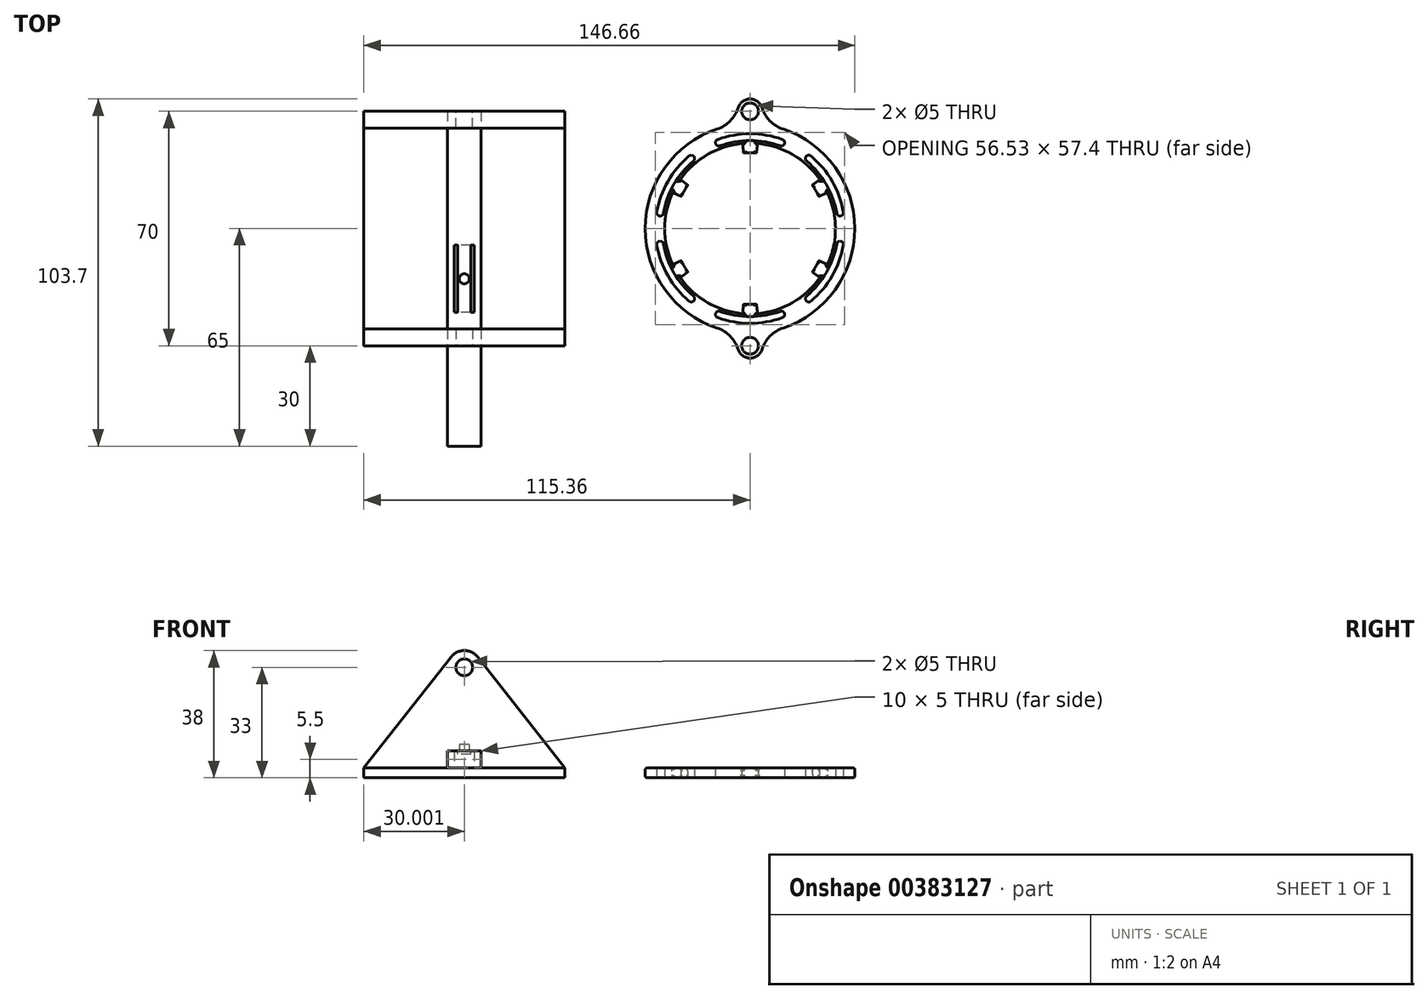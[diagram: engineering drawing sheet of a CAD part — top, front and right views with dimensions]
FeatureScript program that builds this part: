
annotation { "Feature Type Name" : "Feature", "Feature Type Description" : "" }
export const myFeature = defineFeature(function(context is Context, id is Id, definition is map)
    precondition{}
    {
        {
            var Q0;
            Q0=qCreatedBy(makeId("Top.planeOp"),FACE);
            var sketch = newSketch(context, id + "F0", { "sketchPlane" : qUnion([Q0])});
            skArc(sketch, "E0", {"start": v(-2.22, 25.4) * mm, "mid": v(-12.75, 22.08) * mm, "end": v(-20.89, 14.63) * mm});
            skArc(sketch, "E1", {"start": v(-9.89, 29.7) * mm, "mid": v(-31.3, 0) * mm, "end": v(-9.89, -29.7) * mm});
            skArc(sketch, "E2", {"start": v(1.97, 22.56) * mm, "mid": v(0, 22.65) * mm, "end": v(-1.97, 22.56) * mm});
            skArc(sketch, "E3", {"start": v(9, 24.71) * mm, "mid": v(0, 26.3) * mm, "end": v(-9, 24.71) * mm});
            skArc(sketch, "E4", {"start": v(9.68, 26.6) * mm, "mid": v(0, 28.3) * mm, "end": v(-9.68, 26.6) * mm});
            skLineSegment(sketch, "E5", {"start": v(0, 0) * mm, "end": v(-1.97, 22.56) * mm, "construction": true});
            skLineSegment(sketch, "E6", {"start": v(-1.97, 22.56) * mm, "end": v(-2.22, 25.4) * mm});
            skArc(sketch, "E7", {"start": v(-9.68, 26.6) * mm, "mid": v(-10.28, 25.31) * mm, "end": v(-9, 24.71) * mm});
            skLineSegment(sketch, "E8.MirrorCS", {"start": v(1.97, 22.56) * mm, "end": v(2.22, 25.4) * mm});
            skArc(sketch, "E9.MirrorCS", {"start": v(9.68, 26.6) * mm, "mid": v(10.28, 25.31) * mm, "end": v(9, 24.71) * mm});
            skLineSegment(sketch, "E10", {"start": v(-9.34, 25.65) * mm, "end": v(0, 0) * mm, "construction": true});
            skLineSegment(sketch, "E11", {"start": v(0, 0) * mm, "end": v(9.34, 25.65) * mm, "construction": true});
            skLineSegment(sketch, "E12", {"start": v(1.97, 22.56) * mm, "end": v(0, 0) * mm, "construction": true});
            skLineSegment(sketch, "E13.1.0", {"start": v(-20.53, 9.57) * mm, "end": v(-23.11, 10.78) * mm});
            skArc(sketch, "E13.1.1", {"start": v(-18.55, 13) * mm, "mid": v(-19.62, 11.33) * mm, "end": v(-20.53, 9.57) * mm});
            skLineSegment(sketch, "E13.1.2", {"start": v(-18.55, 13) * mm, "end": v(-20.89, 14.63) * mm});
            skArc(sketch, "E13.1.3", {"start": v(-16.9, 20.15) * mm, "mid": v(-22.78, 13.15) * mm, "end": v(-25.9, 4.57) * mm});
            skArc(sketch, "E13.1.4", {"start": v(-27.87, 4.91) * mm, "mid": v(-27.06, 3.76) * mm, "end": v(-25.9, 4.57) * mm});
            skArc(sketch, "E13.1.5", {"start": v(-18.2, 21.68) * mm, "mid": v(-24.5, 14.15) * mm, "end": v(-27.87, 4.91) * mm});
            skArc(sketch, "E13.1.6", {"start": v(-18.2, 21.68) * mm, "mid": v(-16.78, 21.56) * mm, "end": v(-16.9, 20.15) * mm});
            skLineSegment(sketch, "E13.2.0", {"start": v(-18.55, -13) * mm, "end": v(-20.89, -14.63) * mm});
            skArc(sketch, "E13.2.1", {"start": v(-20.53, -9.57) * mm, "mid": v(-19.62, -11.32) * mm, "end": v(-18.55, -13) * mm});
            skLineSegment(sketch, "E13.2.2", {"start": v(-20.53, -9.57) * mm, "end": v(-23.11, -10.78) * mm});
            skArc(sketch, "E13.2.3", {"start": v(-25.9, -4.57) * mm, "mid": v(-22.78, -13.15) * mm, "end": v(-16.9, -20.15) * mm});
            skArc(sketch, "E13.2.4", {"start": v(-18.2, -21.68) * mm, "mid": v(-16.78, -21.56) * mm, "end": v(-16.9, -20.15) * mm});
            skArc(sketch, "E13.2.5", {"start": v(-27.87, -4.91) * mm, "mid": v(-24.5, -14.15) * mm, "end": v(-18.2, -21.68) * mm});
            skArc(sketch, "E13.2.6", {"start": v(-27.87, -4.91) * mm, "mid": v(-27.06, -3.76) * mm, "end": v(-25.9, -4.57) * mm});
            skLineSegment(sketch, "E13.3.0", {"start": v(1.97, -22.56) * mm, "end": v(2.22, -25.4) * mm});
            skArc(sketch, "E13.3.1", {"start": v(-1.97, -22.56) * mm, "mid": v(0, -22.65) * mm, "end": v(1.97, -22.56) * mm});
            skLineSegment(sketch, "E13.3.2", {"start": v(-1.97, -22.56) * mm, "end": v(-2.22, -25.4) * mm});
            skArc(sketch, "E13.3.3", {"start": v(-9, -24.71) * mm, "mid": v(0, -26.3) * mm, "end": v(9, -24.71) * mm});
            skArc(sketch, "E13.3.4", {"start": v(9.68, -26.6) * mm, "mid": v(10.28, -25.31) * mm, "end": v(9, -24.71) * mm});
            skArc(sketch, "E13.3.5", {"start": v(-9.68, -26.6) * mm, "mid": v(0, -28.3) * mm, "end": v(9.68, -26.6) * mm});
            skArc(sketch, "E13.3.6", {"start": v(-9.68, -26.6) * mm, "mid": v(-10.28, -25.31) * mm, "end": v(-9, -24.71) * mm});
            skLineSegment(sketch, "E13.4.0", {"start": v(20.53, -9.57) * mm, "end": v(23.11, -10.78) * mm});
            skArc(sketch, "E13.4.1", {"start": v(18.55, -13) * mm, "mid": v(19.62, -11.33) * mm, "end": v(20.53, -9.57) * mm});
            skLineSegment(sketch, "E13.4.2", {"start": v(18.55, -13) * mm, "end": v(20.89, -14.63) * mm});
            skArc(sketch, "E13.4.3", {"start": v(16.9, -20.15) * mm, "mid": v(22.78, -13.15) * mm, "end": v(25.9, -4.57) * mm});
            skArc(sketch, "E13.4.4", {"start": v(27.87, -4.91) * mm, "mid": v(27.06, -3.76) * mm, "end": v(25.9, -4.57) * mm});
            skArc(sketch, "E13.4.5", {"start": v(18.2, -21.68) * mm, "mid": v(24.5, -14.15) * mm, "end": v(27.87, -4.91) * mm});
            skArc(sketch, "E13.4.6", {"start": v(18.2, -21.68) * mm, "mid": v(16.78, -21.56) * mm, "end": v(16.9, -20.15) * mm});
            skLineSegment(sketch, "E13.5.0", {"start": v(18.55, 13) * mm, "end": v(20.89, 14.63) * mm});
            skArc(sketch, "E13.5.1", {"start": v(20.53, 9.57) * mm, "mid": v(19.62, 11.33) * mm, "end": v(18.55, 13) * mm});
            skLineSegment(sketch, "E13.5.2", {"start": v(20.53, 9.57) * mm, "end": v(23.11, 10.78) * mm});
            skArc(sketch, "E13.5.3", {"start": v(25.9, 4.57) * mm, "mid": v(22.78, 13.15) * mm, "end": v(16.9, 20.15) * mm});
            skArc(sketch, "E13.5.4", {"start": v(18.2, 21.68) * mm, "mid": v(16.78, 21.56) * mm, "end": v(16.9, 20.15) * mm});
            skArc(sketch, "E13.5.5", {"start": v(27.87, 4.91) * mm, "mid": v(24.5, 14.15) * mm, "end": v(18.2, 21.68) * mm});
            skArc(sketch, "E13.5.6", {"start": v(27.87, 4.91) * mm, "mid": v(27.06, 3.76) * mm, "end": v(25.9, 4.57) * mm});
            skArc(sketch, "E14.trimOffspring", {"start": v(20.89, 14.63) * mm, "mid": v(12.75, 22.08) * mm, "end": v(2.22, 25.4) * mm});
            skArc(sketch, "E15.trimOffspring", {"start": v(-23.11, 10.78) * mm, "mid": v(-25.5, 0) * mm, "end": v(-23.11, -10.78) * mm});
            skArc(sketch, "E16.trimOffspring", {"start": v(-20.89, -14.63) * mm, "mid": v(-12.75, -22.08) * mm, "end": v(-2.22, -25.4) * mm});
            skArc(sketch, "E17.trimOffspring", {"start": v(23.11, -10.78) * mm, "mid": v(25.5, 0) * mm, "end": v(23.11, 10.78) * mm});
            skArc(sketch, "E18.trimOffspring", {"start": v(2.22, -25.4) * mm, "mid": v(12.75, -22.08) * mm, "end": v(20.89, -14.63) * mm});
            skArc(sketch, "E19", {"start": v(3.52, 36.13) * mm, "mid": v(0, 38.7) * mm, "end": v(-3.52, 36.13) * mm});
            skCircle(sketch, "E20", {"center": v(0, 35) * mm, "radius": 2.5 * mm});
            skArc(sketch, "E21", {"start": v(-9.89, 29.7) * mm, "mid": v(-5.94, 32.15) * mm, "end": v(-3.52, 36.13) * mm});
            skArc(sketch, "E22.MirrorCS", {"start": v(9.89, 29.7) * mm, "mid": v(5.94, 32.15) * mm, "end": v(3.52, 36.13) * mm});
            skArc(sketch, "E23.MirrorCS", {"start": v(-9.89, -29.7) * mm, "mid": v(-5.94, -32.15) * mm, "end": v(-3.52, -36.13) * mm});
            skArc(sketch, "E24.MirrorCS", {"start": v(3.52, -36.13) * mm, "mid": v(0, -38.7) * mm, "end": v(-3.52, -36.13) * mm});
            skArc(sketch, "E25.MirrorCS", {"start": v(9.89, -29.7) * mm, "mid": v(5.94, -32.15) * mm, "end": v(3.52, -36.13) * mm});
            skCircle(sketch, "E26.MirrorC", {"center": v(0, -35) * mm, "radius": 2.5 * mm});
            skArc(sketch, "E27.trimOffspring", {"start": v(9.89, -29.7) * mm, "mid": v(31.3, 0) * mm, "end": v(9.89, 29.7) * mm});
            skSolve(sketch);
        }
        {
            var Q0;
            Q0=makeQuery(id+"F0.imprint","IMPRINT",FACE,{"disambiguationData":[TD([[makeQuery(id+"F0.imprint","IMPRINT",EDGE,{"derivedFrom":sQuery(id+"F0.wireOp",EDGE,"E0")}),-1.0]])]});
            extrude(context, id + "F1", {"entities" : qUnion([Q0]), "depth" : 1.5 * mm});
        }
        {
            var Q0;
            Q0=makeQuery(id+"F1.opExtrude","CAP_EDGE",EDGE,{"disambiguationData":[OSD([sQuery(id+"F0.wireOp",EDGE,"E6")])],"isStart":true});
            var Q1;
            Q1=makeQuery(id+"F1.opExtrude","CAP_EDGE",EDGE,{"disambiguationData":[OSD([sQuery(id+"F0.wireOp",EDGE,"E8.MirrorCS")])],"isStart":true});
            var Q2;
            Q2=makeQuery(id+"F1.opExtrude","CAP_EDGE",EDGE,{"disambiguationData":[OSD([sQuery(id+"F0.wireOp",EDGE,"E13.5.0")])],"isStart":true});
            var Q3;
            Q3=makeQuery(id+"F1.opExtrude","CAP_EDGE",EDGE,{"disambiguationData":[OSD([sQuery(id+"F0.wireOp",EDGE,"E13.5.2")])],"isStart":true});
            var Q4;
            Q4=makeQuery(id+"F1.opExtrude","CAP_EDGE",EDGE,{"disambiguationData":[OSD([sQuery(id+"F0.wireOp",EDGE,"E13.4.2")])],"isStart":true});
            var Q5;
            Q5=makeQuery(id+"F1.opExtrude","CAP_EDGE",EDGE,{"disambiguationData":[OSD([sQuery(id+"F0.wireOp",EDGE,"E13.3.2")])],"isStart":true});
            var Q6;
            Q6=makeQuery(id+"F1.opExtrude","CAP_EDGE",EDGE,{"disambiguationData":[OSD([sQuery(id+"F0.wireOp",EDGE,"E13.4.0")])],"isStart":true});
            var Q7;
            Q7=makeQuery(id+"F1.opExtrude","CAP_EDGE",EDGE,{"disambiguationData":[OSD([sQuery(id+"F0.wireOp",EDGE,"E13.1.2")])],"isStart":true});
            var Q8;
            Q8=makeQuery(id+"F1.opExtrude","CAP_EDGE",EDGE,{"disambiguationData":[OSD([sQuery(id+"F0.wireOp",EDGE,"E13.2.2")])],"isStart":true});
            var Q9;
            Q9=makeQuery(id+"F1.opExtrude","CAP_EDGE",EDGE,{"disambiguationData":[OSD([sQuery(id+"F0.wireOp",EDGE,"E13.3.0")])],"isStart":true});
            var Q10;
            Q10=makeQuery(id+"F1.opExtrude","CAP_EDGE",EDGE,{"disambiguationData":[OSD([sQuery(id+"F0.wireOp",EDGE,"E13.2.0")])],"isStart":true});
            var Q11;
            Q11=makeQuery(id+"F1.opExtrude","CAP_EDGE",EDGE,{"disambiguationData":[OSD([sQuery(id+"F0.wireOp",EDGE,"E13.1.0")])],"isStart":true});
            fillet(context, id + "F2", {"entities" : qUnion([Q0, Q1, Q2, Q3, Q4, Q5, Q6, Q7, Q8, Q9, Q10, Q11]), "radius" : 1 * mm, "tangentPropagation" : true, "allowEdgeOverflow" : false});
        }
        {
            var Q0;
            Q0=makeQuery(id+"F1.opExtrude","CAP_EDGE",EDGE,{"disambiguationData":[OSD([sQuery(id+"F0.wireOp",EDGE,"E13.3.1")])],"isStart":true});
            var Q1;
            Q1=makeQuery(id+"F1.opExtrude","CAP_EDGE",EDGE,{"disambiguationData":[OSD([sQuery(id+"F0.wireOp",EDGE,"E13.4.1")])],"isStart":true});
            var Q2;
            Q2=makeQuery(id+"F1.opExtrude","CAP_EDGE",EDGE,{"disambiguationData":[OSD([sQuery(id+"F0.wireOp",EDGE,"E13.5.1")])],"isStart":true});
            var Q3;
            Q3=makeQuery(id+"F1.opExtrude","CAP_EDGE",EDGE,{"disambiguationData":[OSD([sQuery(id+"F0.wireOp",EDGE,"E2")])],"isStart":true});
            var Q4;
            Q4=makeQuery(id+"F1.opExtrude","CAP_EDGE",EDGE,{"disambiguationData":[OSD([sQuery(id+"F0.wireOp",EDGE,"E13.1.1")])],"isStart":true});
            var Q5;
            Q5=makeQuery(id+"F1.opExtrude","CAP_EDGE",EDGE,{"disambiguationData":[OSD([sQuery(id+"F0.wireOp",EDGE,"E13.2.1")])],"isStart":true});
            fillet(context, id + "F3", {"entities" : qUnion([Q0, Q1, Q2, Q3, Q4, Q5]), "radius" : 0.2 * mm, "tangentPropagation" : true, "allowEdgeOverflow" : false});
        }
        {
            var Q0;
            Q0=makeQuery(id+"F1.opExtrude","CAP_EDGE",EDGE,{"disambiguationData":[OSD([sQuery(id+"F0.wireOp",EDGE,"E14.trimOffspring")])],"isStart":true});
            var Q1;
            Q1=makeQuery(id+"F1.opExtrude","CAP_EDGE",EDGE,{"disambiguationData":[OSD([sQuery(id+"F0.wireOp",EDGE,"E0")])],"isStart":true});
            var Q2;
            Q2=makeQuery(id+"F1.opExtrude","CAP_EDGE",EDGE,{"disambiguationData":[OSD([sQuery(id+"F0.wireOp",EDGE,"E15.trimOffspring")])],"isStart":true});
            var Q3;
            Q3=makeQuery(id+"F1.opExtrude","CAP_EDGE",EDGE,{"disambiguationData":[OSD([sQuery(id+"F0.wireOp",EDGE,"E16.trimOffspring")])],"isStart":true});
            var Q4;
            Q4=makeQuery(id+"F1.opExtrude","CAP_EDGE",EDGE,{"disambiguationData":[OSD([sQuery(id+"F0.wireOp",EDGE,"E18.trimOffspring")])],"isStart":true});
            var Q5;
            Q5=makeQuery(id+"F1.opExtrude","CAP_EDGE",EDGE,{"disambiguationData":[OSD([sQuery(id+"F0.wireOp",EDGE,"E17.trimOffspring")])],"isStart":true});
            var Q6;
            Q6=makeQuery(id+"F1.opExtrude","CAP_EDGE",EDGE,{"disambiguationData":[OSD([sQuery(id+"F0.wireOp",EDGE,"E13.4.5")])],"isStart":true});
            var Q7;
            Q7=makeQuery(id+"F1.opExtrude","CAP_EDGE",EDGE,{"disambiguationData":[OSD([sQuery(id+"F0.wireOp",EDGE,"E13.3.3")])],"isStart":true});
            var Q8;
            Q8=makeQuery(id+"F1.opExtrude","CAP_EDGE",EDGE,{"disambiguationData":[OSD([sQuery(id+"F0.wireOp",EDGE,"E13.2.5")])],"isStart":true});
            var Q9;
            Q9=makeQuery(id+"F1.opExtrude","CAP_EDGE",EDGE,{"disambiguationData":[OSD([sQuery(id+"F0.wireOp",EDGE,"E13.1.5")])],"isStart":true});
            var Q10;
            Q10=makeQuery(id+"F1.opExtrude","CAP_EDGE",EDGE,{"disambiguationData":[OSD([sQuery(id+"F0.wireOp",EDGE,"E3")])],"isStart":true});
            var Q11;
            Q11=makeQuery(id+"F1.opExtrude","CAP_EDGE",EDGE,{"disambiguationData":[OSD([sQuery(id+"F0.wireOp",EDGE,"E13.5.3")])],"isStart":true});
            fillet(context, id + "F4", {"entities" : qUnion([Q0, Q1, Q2, Q3, Q4, Q5, Q6, Q7, Q8, Q9, Q10, Q11]), "radius" : 0.4 * mm, "tangentPropagation" : true, "allowEdgeOverflow" : false});
        }
        {
            var Q0;
            Q0=makeQuery(id+"F1.opExtrude","SWEPT_EDGE",EDGE,{"disambiguationData":[OSD([sQuery(id+"F0.wireOp",EDGE,"E13.5.0"),sQuery(id+"F0.wireOp",EDGE,"E14.trimOffspring")])]});
            var Q1;
            Q1=makeQuery(id+"F1.opExtrude","SWEPT_EDGE",EDGE,{"disambiguationData":[OSD([sQuery(id+"F0.wireOp",EDGE,"E13.4.0"),sQuery(id+"F0.wireOp",EDGE,"E17.trimOffspring")])]});
            var Q2;
            Q2=makeQuery(id+"F1.opExtrude","SWEPT_EDGE",EDGE,{"disambiguationData":[OSD([sQuery(id+"F0.wireOp",EDGE,"E13.4.2"),sQuery(id+"F0.wireOp",EDGE,"E18.trimOffspring")])]});
            var Q3;
            Q3=makeQuery(id+"F1.opExtrude","SWEPT_EDGE",EDGE,{"disambiguationData":[OSD([sQuery(id+"F0.wireOp",EDGE,"E13.3.2"),sQuery(id+"F0.wireOp",EDGE,"E16.trimOffspring")])]});
            var Q4;
            Q4=makeQuery(id+"F1.opExtrude","SWEPT_EDGE",EDGE,{"disambiguationData":[OSD([sQuery(id+"F0.wireOp",EDGE,"E13.2.2"),sQuery(id+"F0.wireOp",EDGE,"E15.trimOffspring")])]});
            var Q5;
            Q5=makeQuery(id+"F1.opExtrude","SWEPT_EDGE",EDGE,{"disambiguationData":[OSD([sQuery(id+"F0.wireOp",EDGE,"E13.3.0"),sQuery(id+"F0.wireOp",EDGE,"E18.trimOffspring")])]});
            var Q6;
            Q6=makeQuery(id+"F1.opExtrude","SWEPT_EDGE",EDGE,{"disambiguationData":[OSD([sQuery(id+"F0.wireOp",EDGE,"E13.2.0"),sQuery(id+"F0.wireOp",EDGE,"E16.trimOffspring")])]});
            var Q7;
            Q7=makeQuery(id+"F1.opExtrude","SWEPT_EDGE",EDGE,{"disambiguationData":[OSD([sQuery(id+"F0.wireOp",EDGE,"E0"),sQuery(id+"F0.wireOp",EDGE,"E13.1.2")])]});
            var Q8;
            Q8=makeQuery(id+"F1.opExtrude","SWEPT_EDGE",EDGE,{"disambiguationData":[OSD([sQuery(id+"F0.wireOp",EDGE,"E8.MirrorCS"),sQuery(id+"F0.wireOp",EDGE,"E14.trimOffspring")])]});
            var Q9;
            Q9=makeQuery(id+"F1.opExtrude","SWEPT_EDGE",EDGE,{"disambiguationData":[OSD([sQuery(id+"F0.wireOp",EDGE,"E13.1.0"),sQuery(id+"F0.wireOp",EDGE,"E15.trimOffspring")])]});
            var Q10;
            Q10=makeQuery(id+"F1.opExtrude","SWEPT_EDGE",EDGE,{"disambiguationData":[OSD([sQuery(id+"F0.wireOp",EDGE,"E0"),sQuery(id+"F0.wireOp",EDGE,"E6")])]});
            var Q11;
            Q11=makeQuery(id+"F1.opExtrude","SWEPT_EDGE",EDGE,{"disambiguationData":[OSD([sQuery(id+"F0.wireOp",EDGE,"E13.5.2"),sQuery(id+"F0.wireOp",EDGE,"E17.trimOffspring")])]});
            fillet(context, id + "F5", {"entities" : qUnion([Q0, Q1, Q2, Q3, Q4, Q5, Q6, Q7, Q8, Q9, Q10, Q11]), "radius" : 0.5 * mm, "tangentPropagation" : true, "allowEdgeOverflow" : false});
        }
        {
            var Q0;
            Q0=makeQuery(id+"F1.opExtrude","CAP_EDGE",EDGE,{"disambiguationData":[OSD([sQuery(id+"F0.wireOp",EDGE,"E27.trimOffspring")])],"isStart":true});
            var Q1;
            Q1=makeQuery(id+"F1.opExtrude","CAP_EDGE",EDGE,{"disambiguationData":[OSD([sQuery(id+"F0.wireOp",EDGE,"E26.MirrorC")])],"isStart":true});
            var Q2;
            Q2=makeQuery(id+"F1.opExtrude","CAP_EDGE",EDGE,{"disambiguationData":[OSD([sQuery(id+"F0.wireOp",EDGE,"E20")])],"isStart":true});
            fillet(context, id + "F6", {"entities" : qUnion([Q0, Q1, Q2]), "radius" : 0.6 * mm, "tangentPropagation" : true, "allowEdgeOverflow" : false});
        }
        {
            var Q0;
            Q0=makeQuery(id+"F1.opExtrude","SWEPT_BODY",BODY,{"disambiguationData":[OSD([sQuery(id+"F0.wireOp",EDGE,"E0"),sQuery(id+"F0.wireOp",EDGE,"E1"),sQuery(id+"F0.wireOp",EDGE,"E2"),sQuery(id+"F0.wireOp",EDGE,"E3"),sQuery(id+"F0.wireOp",EDGE,"E4"),sQuery(id+"F0.wireOp",EDGE,"E6"),sQuery(id+"F0.wireOp",EDGE,"E7"),sQuery(id+"F0.wireOp",EDGE,"E8.MirrorCS"),sQuery(id+"F0.wireOp",EDGE,"E9.MirrorCS"),sQuery(id+"F0.wireOp",EDGE,"E13.1.0"),sQuery(id+"F0.wireOp",EDGE,"E13.1.1"),sQuery(id+"F0.wireOp",EDGE,"E13.1.2"),sQuery(id+"F0.wireOp",EDGE,"E13.1.3"),sQuery(id+"F0.wireOp",EDGE,"E13.1.4"),sQuery(id+"F0.wireOp",EDGE,"E13.1.5"),sQuery(id+"F0.wireOp",EDGE,"E13.1.6"),sQuery(id+"F0.wireOp",EDGE,"E13.2.0"),sQuery(id+"F0.wireOp",EDGE,"E13.2.1"),sQuery(id+"F0.wireOp",EDGE,"E13.2.2"),sQuery(id+"F0.wireOp",EDGE,"E13.2.3"),sQuery(id+"F0.wireOp",EDGE,"E13.2.4"),sQuery(id+"F0.wireOp",EDGE,"E13.2.5"),sQuery(id+"F0.wireOp",EDGE,"E13.2.6"),sQuery(id+"F0.wireOp",EDGE,"E13.3.0"),sQuery(id+"F0.wireOp",EDGE,"E13.3.1"),sQuery(id+"F0.wireOp",EDGE,"E13.3.2"),sQuery(id+"F0.wireOp",EDGE,"E13.3.3"),sQuery(id+"F0.wireOp",EDGE,"E13.3.4"),sQuery(id+"F0.wireOp",EDGE,"E13.3.5"),sQuery(id+"F0.wireOp",EDGE,"E13.3.6"),sQuery(id+"F0.wireOp",EDGE,"E13.4.0"),sQuery(id+"F0.wireOp",EDGE,"E13.4.1"),sQuery(id+"F0.wireOp",EDGE,"E13.4.2"),sQuery(id+"F0.wireOp",EDGE,"E13.4.3"),sQuery(id+"F0.wireOp",EDGE,"E13.4.4"),sQuery(id+"F0.wireOp",EDGE,"E13.4.5"),sQuery(id+"F0.wireOp",EDGE,"E13.4.6"),sQuery(id+"F0.wireOp",EDGE,"E13.5.0"),sQuery(id+"F0.wireOp",EDGE,"E13.5.1"),sQuery(id+"F0.wireOp",EDGE,"E13.5.2"),sQuery(id+"F0.wireOp",EDGE,"E13.5.3"),sQuery(id+"F0.wireOp",EDGE,"E13.5.4"),sQuery(id+"F0.wireOp",EDGE,"E13.5.5"),sQuery(id+"F0.wireOp",EDGE,"E13.5.6"),sQuery(id+"F0.wireOp",EDGE,"E14.trimOffspring"),sQuery(id+"F0.wireOp",EDGE,"E15.trimOffspring"),sQuery(id+"F0.wireOp",EDGE,"E16.trimOffspring"),sQuery(id+"F0.wireOp",EDGE,"E17.trimOffspring"),sQuery(id+"F0.wireOp",EDGE,"E18.trimOffspring"),sQuery(id+"F0.wireOp",EDGE,"E19"),sQuery(id+"F0.wireOp",EDGE,"E20"),sQuery(id+"F0.wireOp",EDGE,"E21"),sQuery(id+"F0.wireOp",EDGE,"E22.MirrorCS"),sQuery(id+"F0.wireOp",EDGE,"E23.MirrorCS"),sQuery(id+"F0.wireOp",EDGE,"E24.MirrorCS"),sQuery(id+"F0.wireOp",EDGE,"E25.MirrorCS"),sQuery(id+"F0.wireOp",EDGE,"E26.MirrorC"),sQuery(id+"F0.wireOp",EDGE,"E27.trimOffspring")])]});
            var Q1;
            Q1=makeQuery(id+"F1.opExtrude","CAP_FACE",FACE,{"disambiguationData":[OSD([sQuery(id+"F0.wireOp",EDGE,"E0"),sQuery(id+"F0.wireOp",EDGE,"E1"),sQuery(id+"F0.wireOp",EDGE,"E2"),sQuery(id+"F0.wireOp",EDGE,"E3"),sQuery(id+"F0.wireOp",EDGE,"E4"),sQuery(id+"F0.wireOp",EDGE,"E6"),sQuery(id+"F0.wireOp",EDGE,"E7"),sQuery(id+"F0.wireOp",EDGE,"E8.MirrorCS"),sQuery(id+"F0.wireOp",EDGE,"E9.MirrorCS"),sQuery(id+"F0.wireOp",EDGE,"E13.1.0"),sQuery(id+"F0.wireOp",EDGE,"E13.1.1"),sQuery(id+"F0.wireOp",EDGE,"E13.1.2"),sQuery(id+"F0.wireOp",EDGE,"E13.1.3"),sQuery(id+"F0.wireOp",EDGE,"E13.1.4"),sQuery(id+"F0.wireOp",EDGE,"E13.1.5"),sQuery(id+"F0.wireOp",EDGE,"E13.1.6"),sQuery(id+"F0.wireOp",EDGE,"E13.2.0"),sQuery(id+"F0.wireOp",EDGE,"E13.2.1"),sQuery(id+"F0.wireOp",EDGE,"E13.2.2"),sQuery(id+"F0.wireOp",EDGE,"E13.2.3"),sQuery(id+"F0.wireOp",EDGE,"E13.2.4"),sQuery(id+"F0.wireOp",EDGE,"E13.2.5"),sQuery(id+"F0.wireOp",EDGE,"E13.2.6"),sQuery(id+"F0.wireOp",EDGE,"E13.3.0"),sQuery(id+"F0.wireOp",EDGE,"E13.3.1"),sQuery(id+"F0.wireOp",EDGE,"E13.3.2"),sQuery(id+"F0.wireOp",EDGE,"E13.3.3"),sQuery(id+"F0.wireOp",EDGE,"E13.3.4"),sQuery(id+"F0.wireOp",EDGE,"E13.3.5"),sQuery(id+"F0.wireOp",EDGE,"E13.3.6"),sQuery(id+"F0.wireOp",EDGE,"E13.4.0"),sQuery(id+"F0.wireOp",EDGE,"E13.4.1"),sQuery(id+"F0.wireOp",EDGE,"E13.4.2"),sQuery(id+"F0.wireOp",EDGE,"E13.4.3"),sQuery(id+"F0.wireOp",EDGE,"E13.4.4"),sQuery(id+"F0.wireOp",EDGE,"E13.4.5"),sQuery(id+"F0.wireOp",EDGE,"E13.4.6"),sQuery(id+"F0.wireOp",EDGE,"E13.5.0"),sQuery(id+"F0.wireOp",EDGE,"E13.5.1"),sQuery(id+"F0.wireOp",EDGE,"E13.5.2"),sQuery(id+"F0.wireOp",EDGE,"E13.5.3"),sQuery(id+"F0.wireOp",EDGE,"E13.5.4"),sQuery(id+"F0.wireOp",EDGE,"E13.5.5"),sQuery(id+"F0.wireOp",EDGE,"E13.5.6"),sQuery(id+"F0.wireOp",EDGE,"E14.trimOffspring"),sQuery(id+"F0.wireOp",EDGE,"E15.trimOffspring"),sQuery(id+"F0.wireOp",EDGE,"E16.trimOffspring"),sQuery(id+"F0.wireOp",EDGE,"E17.trimOffspring"),sQuery(id+"F0.wireOp",EDGE,"E18.trimOffspring"),sQuery(id+"F0.wireOp",EDGE,"E19"),sQuery(id+"F0.wireOp",EDGE,"E20"),sQuery(id+"F0.wireOp",EDGE,"E21"),sQuery(id+"F0.wireOp",EDGE,"E22.MirrorCS"),sQuery(id+"F0.wireOp",EDGE,"E23.MirrorCS"),sQuery(id+"F0.wireOp",EDGE,"E24.MirrorCS"),sQuery(id+"F0.wireOp",EDGE,"E25.MirrorCS"),sQuery(id+"F0.wireOp",EDGE,"E26.MirrorC"),sQuery(id+"F0.wireOp",EDGE,"E27.trimOffspring")])],"isStart":false});
            mirror(context, id + "F7", {"operationType" : NewBodyOperationType.ADD, "entities" : qUnion([Q0]), "mirrorPlane" : qUnion([Q1])});
        }
        {
            var Q0;
            Q0=qCreatedBy(makeId("Top.planeOp"),FACE);
            var sketch = newSketch(context, id + "F8", { "sketchPlane" : qUnion([Q0])});
            skLineSegment(sketch, "E28.bottom", {"start": v(-115.36, 35) * mm, "end": v(-55.36, 35) * mm});
            skLineSegment(sketch, "E28.top", {"start": v(-115.36, -35) * mm, "end": v(-55.36, -35) * mm});
            skLineSegment(sketch, "E28.left", {"start": v(-115.36, 35) * mm, "end": v(-115.36, -35) * mm});
            skLineSegment(sketch, "E28.right", {"start": v(-55.36, 35) * mm, "end": v(-55.36, -35) * mm});
            skSolve(sketch);
        }
        {
            var Q0;
            Q0=makeQuery(id+"F8.imprint","IMPRINT",FACE,{"disambiguationData":[TD([[makeQuery(id+"F8.imprint","IMPRINT",EDGE,{"derivedFrom":sQuery(id+"F8.wireOp",EDGE,"E28.bottom")}),-1.0]])]});
            extrude(context, id + "F9", {"entities" : qUnion([Q0]), "depth" : 3 * mm});
        }
        {
            var Q0;
            Q0=makeQuery(id+"F9.opExtrude","SWEPT_FACE",FACE,{"disambiguationData":[OSD([sQuery(id+"F8.wireOp",EDGE,"E28.top")])]});
            var sketch = newSketch(context, id + "F10", { "sketchPlane" : qUnion([Q0])});
            skCircle(sketch, "E29", {"center": v(-85.36, 33) * mm, "radius": 2.5 * mm});
            skArc(sketch, "E30", {"start": v(-81.43, 36.1) * mm, "mid": v(-85.36, 38) * mm, "end": v(-89.29, 36.1) * mm});
            skLineSegment(sketch, "E31", {"start": v(-81.43, 36.1) * mm, "end": v(-55.36, 3) * mm});
            skLineSegment(sketch, "E32", {"start": v(-55.36, 3) * mm, "end": v(-115.36, 3) * mm});
            skLineSegment(sketch, "E33", {"start": v(-115.36, 3) * mm, "end": v(-89.29, 36.1) * mm});
            skLineSegment(sketch, "E34.bottom", {"start": v(-90.36, 3) * mm, "end": v(-80.36, 3) * mm});
            skLineSegment(sketch, "E34.top", {"start": v(-90.36, 8) * mm, "end": v(-80.36, 8) * mm});
            skLineSegment(sketch, "E34.left", {"start": v(-90.36, 3) * mm, "end": v(-90.36, 8) * mm});
            skLineSegment(sketch, "E34.right", {"start": v(-80.36, 3) * mm, "end": v(-80.36, 8) * mm});
            skPoint(sketch, "E35", {"position": v(-85.36, 8) * mm});
            skSolve(sketch);
        }
        {
            var Q0;
            Q0=makeQuery(id+"F10.imprint","IMPRINT",FACE,{"disambiguationData":[TD([[makeQuery(id+"F10.imprint","IMPRINT",EDGE,{"derivedFrom":sQuery(id+"F10.wireOp",EDGE,"E29")}),-1.0]])]});
            extrude(context, id + "F11", {"entities" : qUnion([Q0]), "operationType" : NewBodyOperationType.ADD, "oppositeDirection" : true, "depth" : 5 * mm});
        }
        {
            var Q0;
            Q0=makeQuery(id+"F9.opExtrude","SWEPT_BODY",BODY,{"disambiguationData":[OSD([sQuery(id+"F8.wireOp",EDGE,"E28.bottom"),sQuery(id+"F8.wireOp",EDGE,"E28.top"),sQuery(id+"F8.wireOp",EDGE,"E28.left"),sQuery(id+"F8.wireOp",EDGE,"E28.right")])]});
            var Q1;
            Q1=qCreatedBy(makeId("Front.planeOp"),FACE);
            mirror(context, id + "F12", {"operationType" : NewBodyOperationType.ADD, "entities" : qUnion([Q0]), "mirrorPlane" : qUnion([Q1])});
        }
        {
            var Q0;
            Q0=makeQuery(id+"F9.opExtrude","CAP_FACE",FACE,{"disambiguationData":[OSD([sQuery(id+"F8.wireOp",EDGE,"E28.bottom"),sQuery(id+"F8.wireOp",EDGE,"E28.top"),sQuery(id+"F8.wireOp",EDGE,"E28.left"),sQuery(id+"F8.wireOp",EDGE,"E28.right")])],"isStart":false});
            var sketch = newSketch(context, id + "F13", { "sketchPlane" : qUnion([Q0])});
            skLineSegment(sketch, "E36.bottom", {"start": v(-80.36, 35) * mm, "end": v(-90.36, 35) * mm});
            skLineSegment(sketch, "E36.top", {"start": v(-80.36, -65) * mm, "end": v(-90.36, -65) * mm});
            skLineSegment(sketch, "E36.left", {"start": v(-80.36, 35) * mm, "end": v(-80.36, -65) * mm});
            skLineSegment(sketch, "E36.right", {"start": v(-90.36, 35) * mm, "end": v(-90.36, -65) * mm});
            skLineSegment(sketch, "E37.bottom", {"start": v(-82.36, -5) * mm, "end": v(-88.36, -5) * mm});
            skLineSegment(sketch, "E37.top", {"start": v(-82.36, -25) * mm, "end": v(-88.36, -25) * mm});
            skLineSegment(sketch, "E37.left", {"start": v(-82.36, -5) * mm, "end": v(-82.36, -25) * mm});
            skLineSegment(sketch, "E37.right", {"start": v(-88.36, -5) * mm, "end": v(-88.36, -25) * mm});
            skSolve(sketch);
        }
        {
            var Q0;
            Q0=qSketchRegion(id+"F13",true);
            extrude(context, id + "F14", {"entities" : qUnion([Q0]), "depth" : 5 * mm});
        }
        {
            var Q0;
            Q0=makeQuery(id+"F14.opExtrude","CAP_FACE",FACE,{"disambiguationData":[OSD([sQuery(id+"F13.wireOp",EDGE,"E36.bottom"),sQuery(id+"F13.wireOp",EDGE,"E36.top"),sQuery(id+"F13.wireOp",EDGE,"E36.left"),sQuery(id+"F13.wireOp",EDGE,"E36.right"),sQuery(id+"F13.wireOp",EDGE,"E37.bottom"),sQuery(id+"F13.wireOp",EDGE,"E37.top"),sQuery(id+"F13.wireOp",EDGE,"E37.left"),sQuery(id+"F13.wireOp",EDGE,"E37.right")])],"isStart":false});
            var sketch = newSketch(context, id + "F15", { "sketchPlane" : qUnion([Q0])});
            skLineSegment(sketch, "E38.bottom", {"start": v(-87.36, -5) * mm, "end": v(-83.36, -5) * mm});
            skLineSegment(sketch, "E38.top", {"start": v(-87.36, -25) * mm, "end": v(-83.36, -25) * mm});
            skLineSegment(sketch, "E38.left", {"start": v(-87.36, -5) * mm, "end": v(-87.36, -25) * mm});
            skLineSegment(sketch, "E38.right", {"start": v(-83.36, -5) * mm, "end": v(-83.36, -25) * mm});
            skCircle(sketch, "E39", {"center": v(-85.36, -15) * mm, "radius": 1.5 * mm});
            skPoint(sketch, "E39.centerSnap0", {"position": v(-85.36, -25) * mm});
            skPoint(sketch, "E39.centerSnap1", {"position": v(-83.36, -15) * mm});
            skSolve(sketch);
        }
        {
            var Q0;
            Q0=makeQuery(id+"F15.imprint","IMPRINT",FACE,{"disambiguationData":[TD([[makeQuery(id+"F15.imprint","IMPRINT",EDGE,{"derivedFrom":sQuery(id+"F15.wireOp",EDGE,"E39")}),1.0]])]});
            extrude(context, id + "F16", {"entities" : qUnion([Q0]), "depth" : 2 * mm});
        }
        {
            var Q0;
            Q0=makeQuery(id+"F15.imprint","IMPRINT",FACE,{"disambiguationData":[TD([[makeQuery(id+"F15.imprint","IMPRINT",EDGE,{"derivedFrom":sQuery(id+"F15.wireOp",EDGE,"E38.bottom")}),1.0]])]});
            var Q1;
            Q1=makeQuery(id+"F15.imprint","IMPRINT",FACE,{"disambiguationData":[TD([[makeQuery(id+"F15.imprint","IMPRINT",EDGE,{"derivedFrom":sQuery(id+"F15.wireOp",EDGE,"E39")}),1.0]])]});
            extrude(context, id + "F17", {"entities" : qUnion([Q0, Q1]), "operationType" : NewBodyOperationType.ADD, "oppositeDirection" : true, "depth" : 1 * mm});
        }
    });
